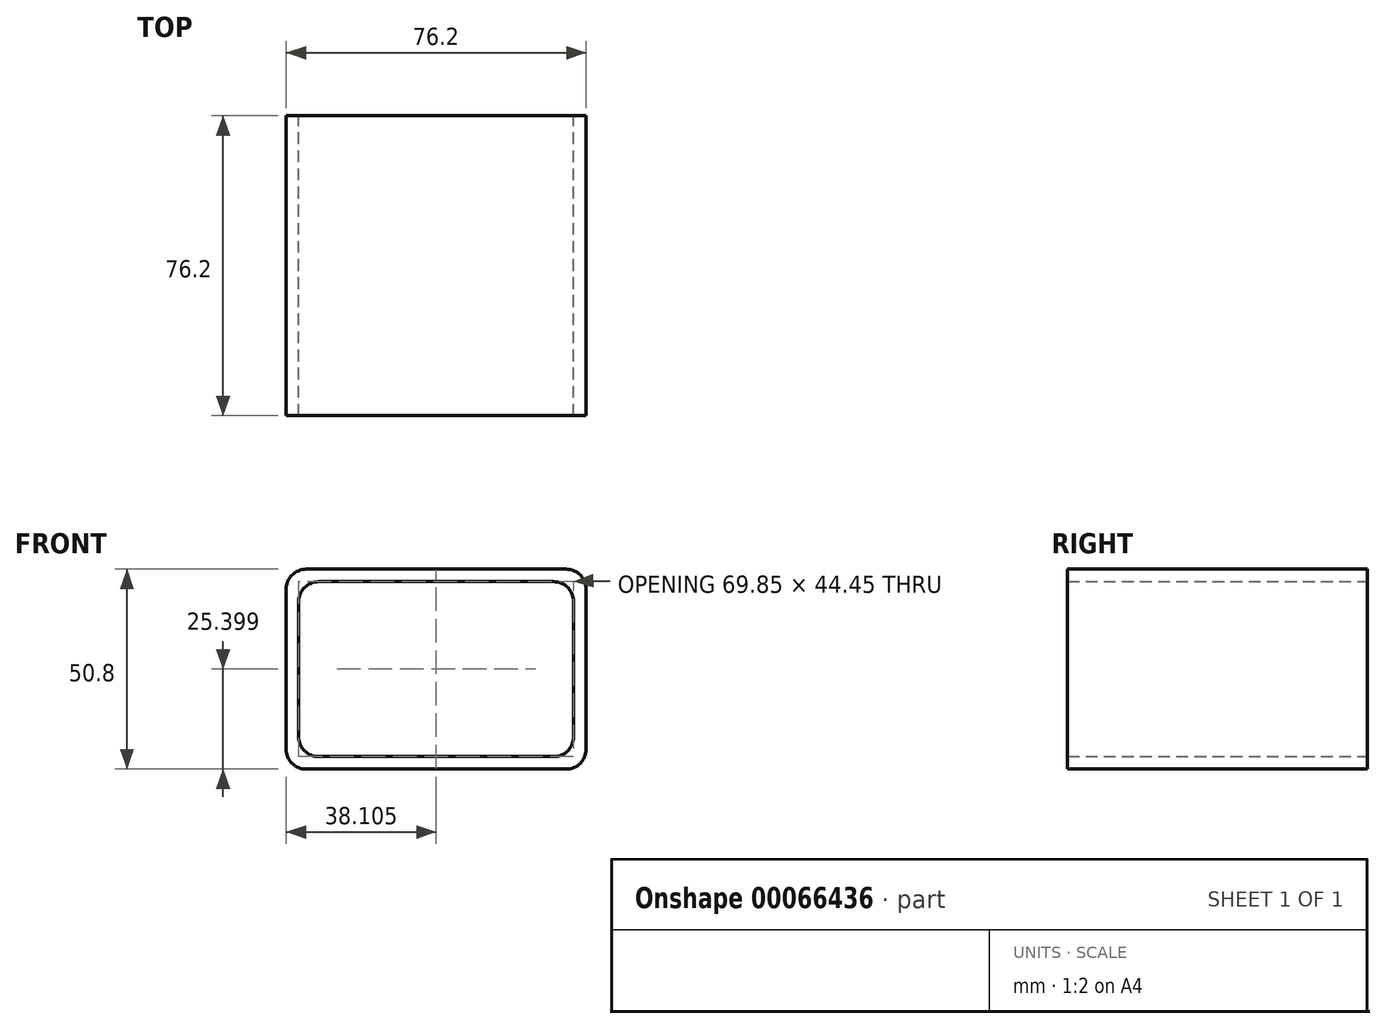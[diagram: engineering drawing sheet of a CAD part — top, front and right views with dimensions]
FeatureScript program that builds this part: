
annotation { "Feature Type Name" : "Feature", "Feature Type Description" : "" }
export const myFeature = defineFeature(function(context is Context, id is Id, definition is map)
    precondition{}
    {
        {
            var Q0;
            Q0=qCreatedBy(makeId("Front.planeOp"),FACE);
            var sketch = newSketch(context, id + "F0", { "sketchPlane" : qUnion([Q0])});
            skLineSegment(sketch, "E0.bottom", {"start": v(-30.94, 20.56) * mm, "end": v(45.26, 20.56) * mm});
            skLineSegment(sketch, "E0.top", {"start": v(-30.94, -30.24) * mm, "end": v(45.26, -30.24) * mm});
            skLineSegment(sketch, "E0.left", {"start": v(-30.94, 20.56) * mm, "end": v(-30.94, -30.24) * mm});
            skLineSegment(sketch, "E0.right", {"start": v(45.26, 20.56) * mm, "end": v(45.26, -30.24) * mm});
            skSolve(sketch);
        }
        {
            var Q0;
            Q0 = qSketchRegion(id + "F0", true);
            extrude(context, id + "F1", {"entities" : qUnion([Q0]), "depth" : 76.2 * mm});
        }
        {
            var Q0;
            Q0=makeQuery(id+"F1.opExtrude","CAP_FACE",FACE,{"disambiguationData":[OSD([sQuery(id+"F0.wireOp",EDGE,"E0.bottom"),sQuery(id+"F0.wireOp",EDGE,"E0.top"),sQuery(id+"F0.wireOp",EDGE,"E0.left"),sQuery(id+"F0.wireOp",EDGE,"E0.right")])],"isStart":false});
            var Q1;
            Q1=makeQuery(id+"F1.opExtrude","CAP_FACE",FACE,{"disambiguationData":[OSD([sQuery(id+"F0.wireOp",EDGE,"E0.bottom"),sQuery(id+"F0.wireOp",EDGE,"E0.top"),sQuery(id+"F0.wireOp",EDGE,"E0.left"),sQuery(id+"F0.wireOp",EDGE,"E0.right")])],"isStart":true});
            shell(context, id + "F2", {"entities" : qUnion([Q0, Q1]), "thickness" : 3.17 * mm});
        }
        {
            var Q0;
            Q0=makeQuery(id+"F1.opExtrude","SWEPT_EDGE",EDGE,{"disambiguationData":[OSD([sQuery(id+"F0.wireOp",EDGE,"E0.bottom"),sQuery(id+"F0.wireOp",EDGE,"E0.right")])]});
            var Q1;
            Q1=makeQuery(id+"F1.opExtrude","SWEPT_EDGE",EDGE,{"disambiguationData":[OSD([sQuery(id+"F0.wireOp",EDGE,"E0.bottom"),sQuery(id+"F0.wireOp",EDGE,"E0.left")])]});
            var Q2;
            Q2=makeQuery(id+"F1.opExtrude","SWEPT_EDGE",EDGE,{"disambiguationData":[OSD([sQuery(id+"F0.wireOp",EDGE,"E0.top"),sQuery(id+"F0.wireOp",EDGE,"E0.right")])]});
            var Q3;
            Q3=makeQuery(id+"F1.opExtrude","SWEPT_EDGE",EDGE,{"disambiguationData":[OSD([sQuery(id+"F0.wireOp",EDGE,"E0.top"),sQuery(id+"F0.wireOp",EDGE,"E0.left")])]});
            var Q4;
            Q4=makeQuery(id+"F2.opShell","OFFSET_EDGE",EDGE,{"disambiguationData":[OSD([sQuery(id+"F0.wireOp",EDGE,"E0.top"),sQuery(id+"F0.wireOp",EDGE,"E0.right")])]});
            var Q5;
            Q5=makeQuery(id+"F2.opShell","OFFSET_EDGE",EDGE,{"disambiguationData":[OSD([sQuery(id+"F0.wireOp",EDGE,"E0.top"),sQuery(id+"F0.wireOp",EDGE,"E0.left")])]});
            var Q6;
            Q6=makeQuery(id+"F2.opShell","OFFSET_EDGE",EDGE,{"disambiguationData":[OSD([sQuery(id+"F0.wireOp",EDGE,"E0.bottom"),sQuery(id+"F0.wireOp",EDGE,"E0.left")])]});
            var Q7;
            Q7=makeQuery(id+"F2.opShell","OFFSET_EDGE",EDGE,{"disambiguationData":[OSD([sQuery(id+"F0.wireOp",EDGE,"E0.bottom"),sQuery(id+"F0.wireOp",EDGE,"E0.right")])]});
            fillet(context, id + "F3", {"entities" : qUnion([Q0, Q1, Q2, Q3, Q4, Q5, Q6, Q7]), "radius" : 5.08 * mm, "tangentPropagation" : true, "allowEdgeOverflow" : false});
        }
    });
